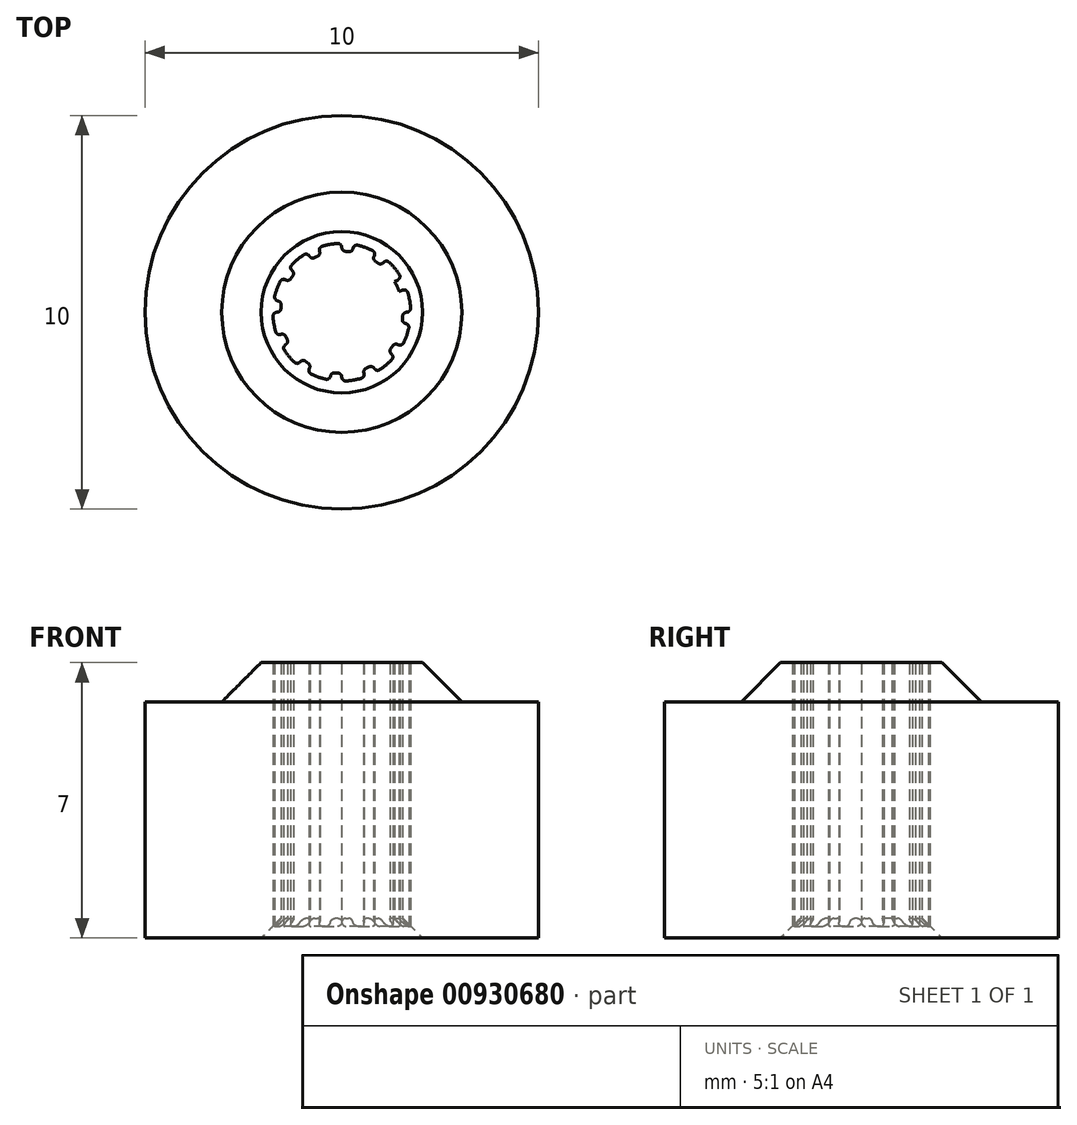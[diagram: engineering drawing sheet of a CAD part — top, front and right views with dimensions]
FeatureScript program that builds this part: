
annotation { "Feature Type Name" : "Feature", "Feature Type Description" : "" }
export const myFeature = defineFeature(function(context is Context, id is Id, definition is map)
    precondition{}
    {
        {
            var Q0;
            Q0=qCreatedBy(makeId("Front.planeOp"),FACE);
            var sketch = newSketch(context, id + "F0", { "sketchPlane" : qUnion([Q0])});
            skLineSegment(sketch, "E0", {"start": v(0, 0) * mm, "end": v(0, 10) * mm, "construction": true});
            skLineSegment(sketch, "E1", {"start": v(1.55, 7) * mm, "end": v(2.05, 7) * mm});
            skLineSegment(sketch, "E2", {"start": v(2.05, 7) * mm, "end": v(3.05, 6) * mm});
            skLineSegment(sketch, "E3", {"start": v(3.05, 6) * mm, "end": v(5, 6) * mm});
            skLineSegment(sketch, "E4", {"start": v(5, 6) * mm, "end": v(5, 0) * mm});
            skLineSegment(sketch, "E5", {"start": v(5, 0) * mm, "end": v(2.05, 0) * mm});
            skLineSegment(sketch, "E6", {"start": v(1.55, 0.5) * mm, "end": v(1.55, 7) * mm});
            skLineSegment(sketch, "E7", {"start": v(2.05, 0) * mm, "end": v(1.55, 0.5) * mm});
            skSolve(sketch);
        }
        {
            var Q0;
            Q0=qSketchRegion(id+"F0",true);
            var Q1;
            Q1=sQuery(id+"F0.wireOp",EDGE,"E0");
            revolve(context, id + "F1", {"entities" : qUnion([Q0]), "axis" : qUnion([Q1]), "revolveType" : RevolveType.FULL});
        }
        {
            var Q0;
            Q0=makeQuery(id+"F1.opRevolve","SWEPT_FACE",FACE,{"disambiguationData":[OSD([sQuery(id+"F0.wireOp",EDGE,"E5")])]});
            var sketch = newSketch(context, id + "F2", { "sketchPlane" : qUnion([Q0])});
            skCircle(sketch, "E8", {"center": v(0, 0) * mm, "radius": 1.5 * mm, "construction": true});
            skArc(sketch, "E9", {"start": v(-1.72, -0.3) * mm, "mid": v(-1.64, -0.6) * mm, "end": v(-1.52, -0.87) * mm});
            skArc(sketch, "E10", {"start": v(-1.34, -0.78) * mm, "mid": v(-1.27, -0.89) * mm, "end": v(-1.19, -1) * mm});
            skLineSegment(sketch, "E11", {"start": v(-1.75, 0) * mm, "end": v(-1.55, 0) * mm});
            skLineSegment(sketch, "E12", {"start": v(-1.72, -0.3) * mm, "end": v(-1.53, -0.27) * mm});
            skLineSegment(sketch, "E13.1.0", {"start": v(-1.34, -1.12) * mm, "end": v(-1.19, -1) * mm});
            skLineSegment(sketch, "E13.1.1", {"start": v(-1.52, -0.88) * mm, "end": v(-1.34, -0.78) * mm});
            skLineSegment(sketch, "E13.2.0", {"start": v(-0.6, -1.64) * mm, "end": v(-0.53, -1.46) * mm});
            skLineSegment(sketch, "E13.2.1", {"start": v(-0.88, -1.52) * mm, "end": v(-0.78, -1.34) * mm});
            skLineSegment(sketch, "E13.3.0", {"start": v(0.3, -1.72) * mm, "end": v(0.27, -1.53) * mm});
            skLineSegment(sketch, "E13.3.1", {"start": v(0, -1.75) * mm, "end": v(0, -1.55) * mm});
            skLineSegment(sketch, "E13.4.0", {"start": v(1.12, -1.34) * mm, "end": v(1, -1.19) * mm});
            skLineSegment(sketch, "E13.4.1", {"start": v(0.88, -1.52) * mm, "end": v(0.78, -1.34) * mm});
            skLineSegment(sketch, "E13.5.0", {"start": v(1.64, -0.6) * mm, "end": v(1.46, -0.53) * mm});
            skLineSegment(sketch, "E13.5.1", {"start": v(1.52, -0.88) * mm, "end": v(1.34, -0.78) * mm});
            skLineSegment(sketch, "E13.6.0", {"start": v(1.72, 0.3) * mm, "end": v(1.53, 0.27) * mm});
            skLineSegment(sketch, "E13.6.1", {"start": v(1.75, 0) * mm, "end": v(1.55, 0) * mm});
            skLineSegment(sketch, "E13.7.0", {"start": v(1.34, 1.12) * mm, "end": v(1.19, 1) * mm});
            skLineSegment(sketch, "E13.7.1", {"start": v(1.52, 0.88) * mm, "end": v(1.34, 0.78) * mm});
            skLineSegment(sketch, "E13.8.0", {"start": v(0.6, 1.64) * mm, "end": v(0.53, 1.46) * mm});
            skLineSegment(sketch, "E13.8.1", {"start": v(0.88, 1.52) * mm, "end": v(0.78, 1.34) * mm});
            skLineSegment(sketch, "E13.9.0", {"start": v(-0.3, 1.72) * mm, "end": v(-0.27, 1.53) * mm});
            skLineSegment(sketch, "E13.9.1", {"start": v(0, 1.75) * mm, "end": v(0, 1.55) * mm});
            skLineSegment(sketch, "E13.10.0", {"start": v(-1.12, 1.34) * mm, "end": v(-1, 1.19) * mm});
            skLineSegment(sketch, "E13.10.1", {"start": v(-0.87, 1.52) * mm, "end": v(-0.77, 1.34) * mm});
            skLineSegment(sketch, "E13.11.0", {"start": v(-1.64, 0.6) * mm, "end": v(-1.46, 0.53) * mm});
            skLineSegment(sketch, "E13.11.1", {"start": v(-1.52, 0.88) * mm, "end": v(-1.34, 0.78) * mm});
            skArc(sketch, "E14.trimOffspring", {"start": v(-1.34, -1.12) * mm, "mid": v(-1.12, -1.34) * mm, "end": v(-0.88, -1.52) * mm});
            skArc(sketch, "E15.trimOffspring", {"start": v(-0.6, -1.64) * mm, "mid": v(-0.3, -1.72) * mm, "end": v(0, -1.75) * mm});
            skArc(sketch, "E16.trimOffspring", {"start": v(0.3, -1.72) * mm, "mid": v(0.6, -1.64) * mm, "end": v(0.87, -1.52) * mm});
            skArc(sketch, "E17.trimOffspring", {"start": v(1.12, -1.34) * mm, "mid": v(1.34, -1.12) * mm, "end": v(1.52, -0.88) * mm});
            skArc(sketch, "E18.trimOffspring", {"start": v(1.64, -0.6) * mm, "mid": v(1.72, -0.3) * mm, "end": v(1.75, 0) * mm});
            skArc(sketch, "E19.trimOffspring", {"start": v(1.72, 0.3) * mm, "mid": v(1.64, 0.6) * mm, "end": v(1.52, 0.87) * mm});
            skArc(sketch, "E20.trimOffspring", {"start": v(1.34, 1.12) * mm, "mid": v(1.12, 1.34) * mm, "end": v(0.88, 1.52) * mm});
            skArc(sketch, "E21.trimOffspring", {"start": v(0.6, 1.64) * mm, "mid": v(0.3, 1.72) * mm, "end": v(0, 1.75) * mm});
            skArc(sketch, "E22.trimOffspring", {"start": v(-0.3, 1.72) * mm, "mid": v(-0.6, 1.64) * mm, "end": v(-0.87, 1.52) * mm});
            skArc(sketch, "E23.trimOffspring", {"start": v(-1.12, 1.34) * mm, "mid": v(-1.34, 1.12) * mm, "end": v(-1.52, 0.88) * mm});
            skArc(sketch, "E24.trimOffspring", {"start": v(-1.64, 0.6) * mm, "mid": v(-1.72, 0.3) * mm, "end": v(-1.75, 0) * mm});
            skArc(sketch, "E25.trimOffspring", {"start": v(-0.78, -1.34) * mm, "mid": v(-0.66, -1.4) * mm, "end": v(-0.53, -1.46) * mm});
            skArc(sketch, "E26.trimOffspring", {"start": v(0, -1.55) * mm, "mid": v(0.14, -1.54) * mm, "end": v(0.27, -1.53) * mm});
            skArc(sketch, "E27.trimOffspring", {"start": v(0.77, -1.34) * mm, "mid": v(0.89, -1.27) * mm, "end": v(1, -1.19) * mm});
            skArc(sketch, "E28.trimOffspring", {"start": v(1.34, -0.78) * mm, "mid": v(1.4, -0.66) * mm, "end": v(1.46, -0.53) * mm});
            skArc(sketch, "E29.trimOffspring", {"start": v(1.55, 0) * mm, "mid": v(1.54, 0.14) * mm, "end": v(1.53, 0.27) * mm});
            skArc(sketch, "E30.trimOffspring", {"start": v(1.34, 0.77) * mm, "mid": v(1.27, 0.89) * mm, "end": v(1.19, 1) * mm});
            skArc(sketch, "E31.trimOffspring", {"start": v(0.78, 1.34) * mm, "mid": v(0.66, 1.4) * mm, "end": v(0.53, 1.46) * mm});
            skArc(sketch, "E32.trimOffspring", {"start": v(0, 1.55) * mm, "mid": v(-0.14, 1.54) * mm, "end": v(-0.27, 1.53) * mm});
            skArc(sketch, "E33.trimOffspring", {"start": v(-0.77, 1.34) * mm, "mid": v(-0.89, 1.27) * mm, "end": v(-1, 1.19) * mm});
            skArc(sketch, "E34.trimOffspring", {"start": v(-1.34, 0.78) * mm, "mid": v(-1.4, 0.66) * mm, "end": v(-1.46, 0.53) * mm});
            skArc(sketch, "E35.trimOffspring", {"start": v(-1.55, 0) * mm, "mid": v(-1.54, -0.14) * mm, "end": v(-1.53, -0.27) * mm});
            skSolve(sketch);
        }
        {
            var Q0;
            Q0=qSketchRegion(id+"F2",true);
            var Q1;
            Q1=makeQuery(id+"F1.opRevolve","SWEPT_FACE",FACE,{"disambiguationData":[OSD([sQuery(id+"F0.wireOp",EDGE,"E1")])]});
            extrude(context, id + "F3", {"entities" : qUnion([Q0]), "operationType" : NewBodyOperationType.REMOVE, "endBound" : BoundingType.UP_TO_SURFACE, "oppositeDirection" : true, "depth" : 25 * mm, "endBoundEntityFace" : qUnion([Q1]), "offsetDistance" : 25 * mm});
        }
        {
            var Q0;
            Q0=makeQuery(id+"F3.boolean.opBoolean","COPY",EDGE,{"derivedFrom":makeQuery(id+"F3.opExtrude","SWEPT_EDGE",EDGE,{"disambiguationData":[OSD([sQuery(id+"F2.wireOp",EDGE,"E13.4.0"),sQuery(id+"F2.wireOp",EDGE,"E17.trimOffspring")])]})});
            var Q1;
            Q1=makeQuery(id+"F3.boolean.opBoolean","COPY",EDGE,{"derivedFrom":makeQuery(id+"F3.opExtrude","SWEPT_EDGE",EDGE,{"disambiguationData":[OSD([sQuery(id+"F2.wireOp",EDGE,"E13.4.1"),sQuery(id+"F2.wireOp",EDGE,"E16.trimOffspring")])]})});
            var Q2;
            Q2=makeQuery(id+"F3.boolean.opBoolean","COPY",EDGE,{"derivedFrom":makeQuery(id+"F3.opExtrude","SWEPT_EDGE",EDGE,{"disambiguationData":[OSD([sQuery(id+"F2.wireOp",EDGE,"E13.4.0"),sQuery(id+"F2.wireOp",EDGE,"E27.trimOffspring")])]})});
            var Q3;
            Q3=makeQuery(id+"F3.boolean.opBoolean","COPY",EDGE,{"derivedFrom":makeQuery(id+"F3.opExtrude","SWEPT_EDGE",EDGE,{"disambiguationData":[OSD([sQuery(id+"F2.wireOp",EDGE,"E13.4.1"),sQuery(id+"F2.wireOp",EDGE,"E27.trimOffspring")])]})});
            var Q4;
            Q4=makeQuery(id+"F3.boolean.opBoolean","COPY",EDGE,{"derivedFrom":makeQuery(id+"F3.opExtrude","SWEPT_EDGE",EDGE,{"disambiguationData":[OSD([sQuery(id+"F2.wireOp",EDGE,"E13.3.0"),sQuery(id+"F2.wireOp",EDGE,"E16.trimOffspring")])]})});
            var Q5;
            Q5=makeQuery(id+"F3.boolean.opBoolean","COPY",EDGE,{"derivedFrom":makeQuery(id+"F3.opExtrude","SWEPT_EDGE",EDGE,{"disambiguationData":[OSD([sQuery(id+"F2.wireOp",EDGE,"E13.3.0"),sQuery(id+"F2.wireOp",EDGE,"E26.trimOffspring")])]})});
            var Q6;
            Q6=makeQuery(id+"F3.boolean.opBoolean","COPY",EDGE,{"derivedFrom":makeQuery(id+"F3.opExtrude","SWEPT_EDGE",EDGE,{"disambiguationData":[OSD([sQuery(id+"F2.wireOp",EDGE,"E13.3.1"),sQuery(id+"F2.wireOp",EDGE,"E26.trimOffspring")])]})});
            var Q7;
            Q7=makeQuery(id+"F3.boolean.opBoolean","COPY",EDGE,{"derivedFrom":makeQuery(id+"F3.opExtrude","SWEPT_EDGE",EDGE,{"disambiguationData":[OSD([sQuery(id+"F2.wireOp",EDGE,"E13.3.1"),sQuery(id+"F2.wireOp",EDGE,"E15.trimOffspring")])]})});
            var Q8;
            Q8=makeQuery(id+"F3.boolean.opBoolean","COPY",EDGE,{"derivedFrom":makeQuery(id+"F3.opExtrude","SWEPT_EDGE",EDGE,{"disambiguationData":[OSD([sQuery(id+"F2.wireOp",EDGE,"E13.2.0"),sQuery(id+"F2.wireOp",EDGE,"E15.trimOffspring")])]})});
            var Q9;
            Q9=makeQuery(id+"F3.boolean.opBoolean","COPY",EDGE,{"derivedFrom":makeQuery(id+"F3.opExtrude","SWEPT_EDGE",EDGE,{"disambiguationData":[OSD([sQuery(id+"F2.wireOp",EDGE,"E13.2.0"),sQuery(id+"F2.wireOp",EDGE,"E25.trimOffspring")])]})});
            var Q10;
            Q10=makeQuery(id+"F3.boolean.opBoolean","COPY",EDGE,{"derivedFrom":makeQuery(id+"F3.opExtrude","SWEPT_EDGE",EDGE,{"disambiguationData":[OSD([sQuery(id+"F2.wireOp",EDGE,"E13.2.1"),sQuery(id+"F2.wireOp",EDGE,"E25.trimOffspring")])]})});
            var Q11;
            Q11=makeQuery(id+"F3.boolean.opBoolean","COPY",EDGE,{"derivedFrom":makeQuery(id+"F3.opExtrude","SWEPT_EDGE",EDGE,{"disambiguationData":[OSD([sQuery(id+"F2.wireOp",EDGE,"E13.2.1"),sQuery(id+"F2.wireOp",EDGE,"E14.trimOffspring")])]})});
            var Q12;
            Q12=makeQuery(id+"F3.boolean.opBoolean","COPY",EDGE,{"derivedFrom":makeQuery(id+"F3.opExtrude","SWEPT_EDGE",EDGE,{"disambiguationData":[OSD([sQuery(id+"F2.wireOp",EDGE,"E13.1.0"),sQuery(id+"F2.wireOp",EDGE,"E14.trimOffspring")])]})});
            var Q13;
            Q13=makeQuery(id+"F3.boolean.opBoolean","COPY",EDGE,{"derivedFrom":makeQuery(id+"F3.opExtrude","SWEPT_EDGE",EDGE,{"disambiguationData":[OSD([sQuery(id+"F2.wireOp",EDGE,"E10"),sQuery(id+"F2.wireOp",EDGE,"E13.1.0")])]})});
            var Q14;
            Q14=makeQuery(id+"F3.boolean.opBoolean","COPY",EDGE,{"derivedFrom":makeQuery(id+"F3.opExtrude","SWEPT_EDGE",EDGE,{"disambiguationData":[OSD([sQuery(id+"F2.wireOp",EDGE,"E10"),sQuery(id+"F2.wireOp",EDGE,"E13.1.1")])]})});
            var Q15;
            Q15=makeQuery(id+"F3.boolean.opBoolean","COPY",EDGE,{"derivedFrom":makeQuery(id+"F3.opExtrude","SWEPT_EDGE",EDGE,{"disambiguationData":[OSD([sQuery(id+"F2.wireOp",EDGE,"E9"),sQuery(id+"F2.wireOp",EDGE,"E13.1.1")])]})});
            var Q16;
            Q16=makeQuery(id+"F3.boolean.opBoolean","COPY",EDGE,{"derivedFrom":makeQuery(id+"F3.opExtrude","SWEPT_EDGE",EDGE,{"disambiguationData":[OSD([sQuery(id+"F2.wireOp",EDGE,"E9"),sQuery(id+"F2.wireOp",EDGE,"E12")])]})});
            var Q17;
            Q17=makeQuery(id+"F3.boolean.opBoolean","COPY",EDGE,{"derivedFrom":makeQuery(id+"F3.opExtrude","SWEPT_EDGE",EDGE,{"disambiguationData":[OSD([sQuery(id+"F2.wireOp",EDGE,"E12"),sQuery(id+"F2.wireOp",EDGE,"E35.trimOffspring")])]})});
            var Q18;
            Q18=makeQuery(id+"F3.boolean.opBoolean","COPY",EDGE,{"derivedFrom":makeQuery(id+"F3.opExtrude","SWEPT_EDGE",EDGE,{"disambiguationData":[OSD([sQuery(id+"F2.wireOp",EDGE,"E11"),sQuery(id+"F2.wireOp",EDGE,"E35.trimOffspring")])]})});
            var Q19;
            Q19=makeQuery(id+"F3.boolean.opBoolean","COPY",EDGE,{"derivedFrom":makeQuery(id+"F3.opExtrude","SWEPT_EDGE",EDGE,{"disambiguationData":[OSD([sQuery(id+"F2.wireOp",EDGE,"E11"),sQuery(id+"F2.wireOp",EDGE,"E24.trimOffspring")])]})});
            var Q20;
            Q20=makeQuery(id+"F3.boolean.opBoolean","COPY",EDGE,{"derivedFrom":makeQuery(id+"F3.opExtrude","SWEPT_EDGE",EDGE,{"disambiguationData":[OSD([sQuery(id+"F2.wireOp",EDGE,"E13.11.0"),sQuery(id+"F2.wireOp",EDGE,"E24.trimOffspring")])]})});
            var Q21;
            Q21=makeQuery(id+"F3.boolean.opBoolean","COPY",EDGE,{"derivedFrom":makeQuery(id+"F3.opExtrude","SWEPT_EDGE",EDGE,{"disambiguationData":[OSD([sQuery(id+"F2.wireOp",EDGE,"E13.11.0"),sQuery(id+"F2.wireOp",EDGE,"E34.trimOffspring")])]})});
            var Q22;
            Q22=makeQuery(id+"F3.boolean.opBoolean","COPY",EDGE,{"derivedFrom":makeQuery(id+"F3.opExtrude","SWEPT_EDGE",EDGE,{"disambiguationData":[OSD([sQuery(id+"F2.wireOp",EDGE,"E13.11.1"),sQuery(id+"F2.wireOp",EDGE,"E34.trimOffspring")])]})});
            var Q23;
            Q23=makeQuery(id+"F3.boolean.opBoolean","COPY",EDGE,{"derivedFrom":makeQuery(id+"F3.opExtrude","SWEPT_EDGE",EDGE,{"disambiguationData":[OSD([sQuery(id+"F2.wireOp",EDGE,"E13.11.1"),sQuery(id+"F2.wireOp",EDGE,"E23.trimOffspring")])]})});
            var Q24;
            Q24=makeQuery(id+"F3.boolean.opBoolean","COPY",EDGE,{"derivedFrom":makeQuery(id+"F3.opExtrude","SWEPT_EDGE",EDGE,{"disambiguationData":[OSD([sQuery(id+"F2.wireOp",EDGE,"E13.10.0"),sQuery(id+"F2.wireOp",EDGE,"E23.trimOffspring")])]})});
            var Q25;
            Q25=makeQuery(id+"F3.boolean.opBoolean","COPY",EDGE,{"derivedFrom":makeQuery(id+"F3.opExtrude","SWEPT_EDGE",EDGE,{"disambiguationData":[OSD([sQuery(id+"F2.wireOp",EDGE,"E13.10.0"),sQuery(id+"F2.wireOp",EDGE,"E33.trimOffspring")])]})});
            var Q26;
            Q26=makeQuery(id+"F3.boolean.opBoolean","COPY",EDGE,{"derivedFrom":makeQuery(id+"F3.opExtrude","SWEPT_EDGE",EDGE,{"disambiguationData":[OSD([sQuery(id+"F2.wireOp",EDGE,"E13.10.1"),sQuery(id+"F2.wireOp",EDGE,"E33.trimOffspring")])]})});
            var Q27;
            Q27=makeQuery(id+"F3.boolean.opBoolean","COPY",EDGE,{"derivedFrom":makeQuery(id+"F3.opExtrude","SWEPT_EDGE",EDGE,{"disambiguationData":[OSD([sQuery(id+"F2.wireOp",EDGE,"E13.10.1"),sQuery(id+"F2.wireOp",EDGE,"E22.trimOffspring")])]})});
            var Q28;
            Q28=makeQuery(id+"F3.boolean.opBoolean","COPY",EDGE,{"derivedFrom":makeQuery(id+"F3.opExtrude","SWEPT_EDGE",EDGE,{"disambiguationData":[OSD([sQuery(id+"F2.wireOp",EDGE,"E13.9.0"),sQuery(id+"F2.wireOp",EDGE,"E22.trimOffspring")])]})});
            var Q29;
            Q29=makeQuery(id+"F3.boolean.opBoolean","COPY",EDGE,{"derivedFrom":makeQuery(id+"F3.opExtrude","SWEPT_EDGE",EDGE,{"disambiguationData":[OSD([sQuery(id+"F2.wireOp",EDGE,"E13.9.0"),sQuery(id+"F2.wireOp",EDGE,"E32.trimOffspring")])]})});
            var Q30;
            Q30=makeQuery(id+"F3.boolean.opBoolean","COPY",EDGE,{"derivedFrom":makeQuery(id+"F3.opExtrude","SWEPT_EDGE",EDGE,{"disambiguationData":[OSD([sQuery(id+"F2.wireOp",EDGE,"E13.9.1"),sQuery(id+"F2.wireOp",EDGE,"E32.trimOffspring")])]})});
            var Q31;
            Q31=makeQuery(id+"F3.boolean.opBoolean","COPY",EDGE,{"derivedFrom":makeQuery(id+"F3.opExtrude","SWEPT_EDGE",EDGE,{"disambiguationData":[OSD([sQuery(id+"F2.wireOp",EDGE,"E13.9.1"),sQuery(id+"F2.wireOp",EDGE,"E21.trimOffspring")])]})});
            var Q32;
            Q32=makeQuery(id+"F3.boolean.opBoolean","COPY",EDGE,{"derivedFrom":makeQuery(id+"F3.opExtrude","SWEPT_EDGE",EDGE,{"disambiguationData":[OSD([sQuery(id+"F2.wireOp",EDGE,"E13.8.0"),sQuery(id+"F2.wireOp",EDGE,"E21.trimOffspring")])]})});
            var Q33;
            Q33=makeQuery(id+"F3.boolean.opBoolean","COPY",EDGE,{"derivedFrom":makeQuery(id+"F3.opExtrude","SWEPT_EDGE",EDGE,{"disambiguationData":[OSD([sQuery(id+"F2.wireOp",EDGE,"E13.8.0"),sQuery(id+"F2.wireOp",EDGE,"E31.trimOffspring")])]})});
            var Q34;
            Q34=makeQuery(id+"F3.boolean.opBoolean","COPY",EDGE,{"derivedFrom":makeQuery(id+"F3.opExtrude","SWEPT_EDGE",EDGE,{"disambiguationData":[OSD([sQuery(id+"F2.wireOp",EDGE,"E13.8.1"),sQuery(id+"F2.wireOp",EDGE,"E31.trimOffspring")])]})});
            var Q35;
            Q35=makeQuery(id+"F3.boolean.opBoolean","COPY",EDGE,{"derivedFrom":makeQuery(id+"F3.opExtrude","SWEPT_EDGE",EDGE,{"disambiguationData":[OSD([sQuery(id+"F2.wireOp",EDGE,"E13.8.1"),sQuery(id+"F2.wireOp",EDGE,"E20.trimOffspring")])]})});
            var Q36;
            Q36=makeQuery(id+"F3.boolean.opBoolean","COPY",EDGE,{"derivedFrom":makeQuery(id+"F3.opExtrude","SWEPT_EDGE",EDGE,{"disambiguationData":[OSD([sQuery(id+"F2.wireOp",EDGE,"E13.7.0"),sQuery(id+"F2.wireOp",EDGE,"E20.trimOffspring")])]})});
            var Q37;
            Q37=makeQuery(id+"F3.boolean.opBoolean","COPY",EDGE,{"derivedFrom":makeQuery(id+"F3.opExtrude","SWEPT_EDGE",EDGE,{"disambiguationData":[OSD([sQuery(id+"F2.wireOp",EDGE,"E13.7.0"),sQuery(id+"F2.wireOp",EDGE,"E30.trimOffspring")])]})});
            var Q38;
            Q38=makeQuery(id+"F3.boolean.opBoolean","COPY",EDGE,{"derivedFrom":makeQuery(id+"F3.opExtrude","SWEPT_EDGE",EDGE,{"disambiguationData":[OSD([sQuery(id+"F2.wireOp",EDGE,"E13.7.1"),sQuery(id+"F2.wireOp",EDGE,"E30.trimOffspring")])]})});
            var Q39;
            Q39=makeQuery(id+"F3.boolean.opBoolean","COPY",EDGE,{"derivedFrom":makeQuery(id+"F3.opExtrude","SWEPT_EDGE",EDGE,{"disambiguationData":[OSD([sQuery(id+"F2.wireOp",EDGE,"E13.7.1"),sQuery(id+"F2.wireOp",EDGE,"E19.trimOffspring")])]})});
            var Q40;
            Q40=makeQuery(id+"F3.boolean.opBoolean","COPY",EDGE,{"derivedFrom":makeQuery(id+"F3.opExtrude","SWEPT_EDGE",EDGE,{"disambiguationData":[OSD([sQuery(id+"F2.wireOp",EDGE,"E13.6.0"),sQuery(id+"F2.wireOp",EDGE,"E19.trimOffspring")])]})});
            var Q41;
            Q41=makeQuery(id+"F3.boolean.opBoolean","COPY",EDGE,{"derivedFrom":makeQuery(id+"F3.opExtrude","SWEPT_EDGE",EDGE,{"disambiguationData":[OSD([sQuery(id+"F2.wireOp",EDGE,"E13.6.0"),sQuery(id+"F2.wireOp",EDGE,"E29.trimOffspring")])]})});
            var Q42;
            Q42=makeQuery(id+"F3.boolean.opBoolean","COPY",EDGE,{"derivedFrom":makeQuery(id+"F3.opExtrude","SWEPT_EDGE",EDGE,{"disambiguationData":[OSD([sQuery(id+"F2.wireOp",EDGE,"E13.6.1"),sQuery(id+"F2.wireOp",EDGE,"E29.trimOffspring")])]})});
            var Q43;
            Q43=makeQuery(id+"F3.boolean.opBoolean","COPY",EDGE,{"derivedFrom":makeQuery(id+"F3.opExtrude","SWEPT_EDGE",EDGE,{"disambiguationData":[OSD([sQuery(id+"F2.wireOp",EDGE,"E13.6.1"),sQuery(id+"F2.wireOp",EDGE,"E18.trimOffspring")])]})});
            var Q44;
            Q44=makeQuery(id+"F3.boolean.opBoolean","COPY",EDGE,{"derivedFrom":makeQuery(id+"F3.opExtrude","SWEPT_EDGE",EDGE,{"disambiguationData":[OSD([sQuery(id+"F2.wireOp",EDGE,"E13.5.0"),sQuery(id+"F2.wireOp",EDGE,"E18.trimOffspring")])]})});
            var Q45;
            Q45=makeQuery(id+"F3.boolean.opBoolean","COPY",EDGE,{"derivedFrom":makeQuery(id+"F3.opExtrude","SWEPT_EDGE",EDGE,{"disambiguationData":[OSD([sQuery(id+"F2.wireOp",EDGE,"E13.5.0"),sQuery(id+"F2.wireOp",EDGE,"E28.trimOffspring")])]})});
            var Q46;
            Q46=makeQuery(id+"F3.boolean.opBoolean","COPY",EDGE,{"derivedFrom":makeQuery(id+"F3.opExtrude","SWEPT_EDGE",EDGE,{"disambiguationData":[OSD([sQuery(id+"F2.wireOp",EDGE,"E13.5.1"),sQuery(id+"F2.wireOp",EDGE,"E28.trimOffspring")])]})});
            var Q47;
            Q47=makeQuery(id+"F3.boolean.opBoolean","COPY",EDGE,{"derivedFrom":makeQuery(id+"F3.opExtrude","SWEPT_EDGE",EDGE,{"disambiguationData":[OSD([sQuery(id+"F2.wireOp",EDGE,"E13.5.1"),sQuery(id+"F2.wireOp",EDGE,"E17.trimOffspring")])]})});
            fillet(context, id + "F4", {"entities" : qUnion([Q0, Q1, Q2, Q3, Q4, Q5, Q6, Q7, Q8, Q9, Q10, Q11, Q12, Q13, Q14, Q15, Q16, Q17, Q18, Q19, Q20, Q21, Q22, Q23, Q24, Q25, Q26, Q27, Q28, Q29, Q30, Q31, Q32, Q33, Q34, Q35, Q36, Q37, Q38, Q39, Q40, Q41, Q42, Q43, Q44, Q45, Q46, Q47]), "radius" : 0.1 * mm, "tangentPropagation" : true, "allowEdgeOverflow" : false});
        }
    });
